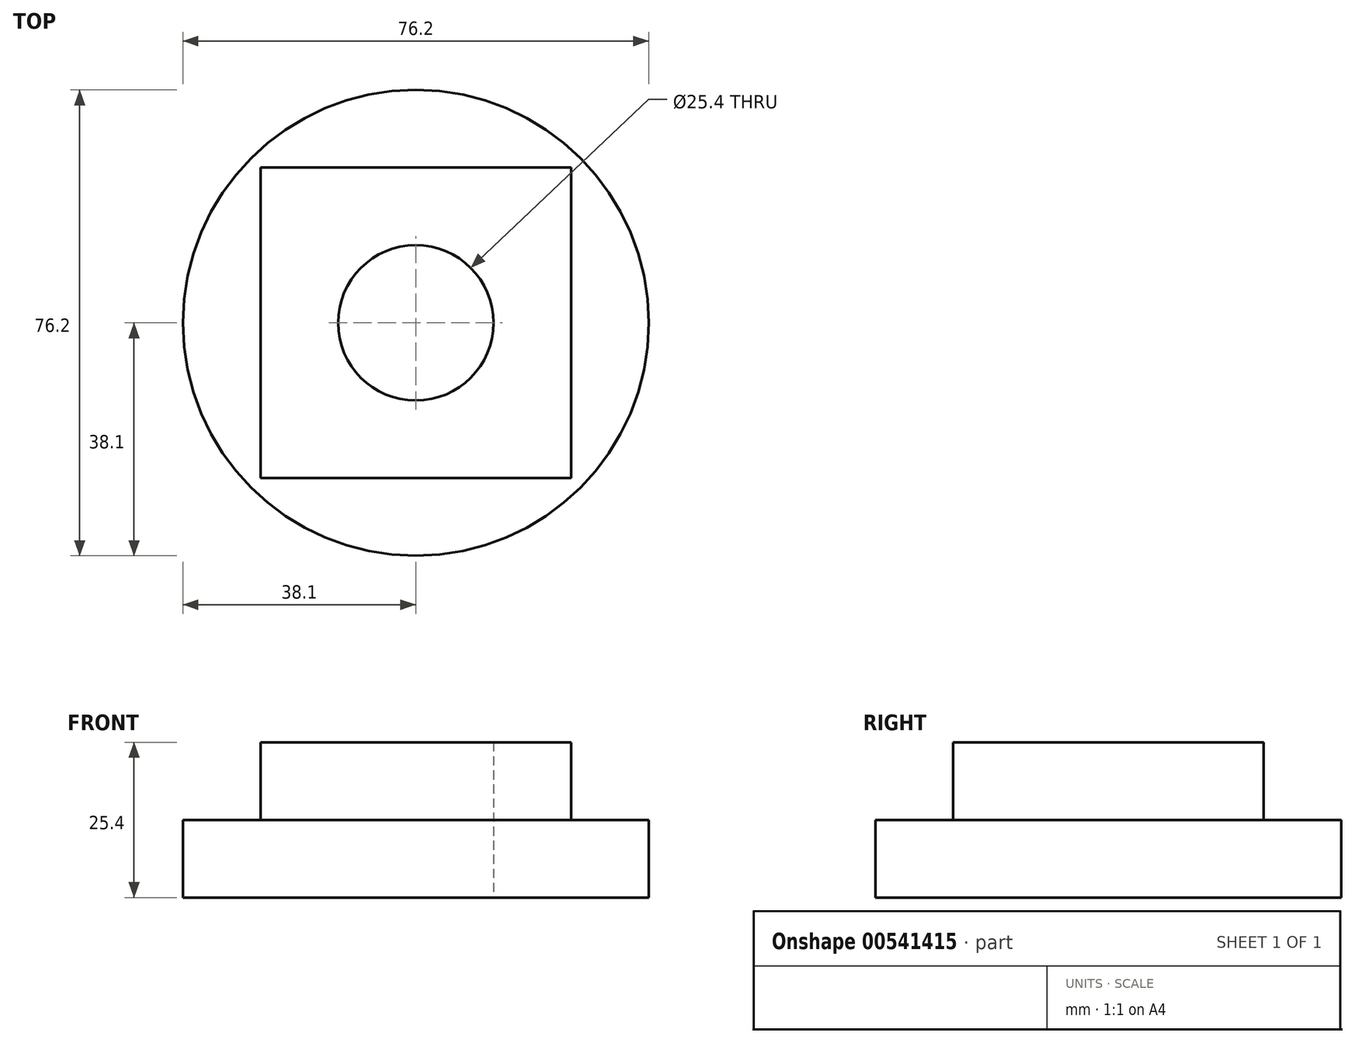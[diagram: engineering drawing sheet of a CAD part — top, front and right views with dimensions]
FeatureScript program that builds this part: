
annotation { "Feature Type Name" : "Feature", "Feature Type Description" : "" }
export const myFeature = defineFeature(function(context is Context, id is Id, definition is map)
    precondition{}
    {
        {
            var Q0;
            Q0=qCreatedBy(makeId("Top.planeOp"),FACE);
            var sketch = newSketch(context, id + "F0", { "sketchPlane" : qUnion([Q0])});
            skCircle(sketch, "E0", {"center": v(0, 0) * mm, "radius": 38.1 * mm});
            skLineSegment(sketch, "E1.bottom", {"start": v(-25.4, 25.4) * mm, "end": v(25.4, 25.4) * mm});
            skLineSegment(sketch, "E1.top", {"start": v(-25.4, -25.4) * mm, "end": v(25.4, -25.4) * mm});
            skLineSegment(sketch, "E1.left", {"start": v(-25.4, 25.4) * mm, "end": v(-25.4, -25.4) * mm});
            skLineSegment(sketch, "E1.right", {"start": v(25.4, 25.4) * mm, "end": v(25.4, -25.4) * mm});
            skCircle(sketch, "E2", {"center": v(0, 0) * mm, "radius": 12.7 * mm});
            skSolve(sketch);
        }
        {
            var Q0;
            Q0=makeQuery(id+"F0.imprint","IMPRINT",FACE,{"disambiguationData":[TD([[makeQuery(id+"F0.imprint","IMPRINT",EDGE,{"derivedFrom":sQuery(id+"F0.wireOp",EDGE,"E0")}),1.0]])]});
            var Q1;
            Q1=makeQuery(id+"F0.imprint","IMPRINT",FACE,{"disambiguationData":[TD([[makeQuery(id+"F0.imprint","IMPRINT",EDGE,{"derivedFrom":sQuery(id+"F0.wireOp",EDGE,"E1.bottom")}),-1.0]])]});
            var Q2;
            Q2=makeQuery(id+"F0.imprint","IMPRINT",FACE,{"disambiguationData":[TD([[makeQuery(id+"F0.imprint","IMPRINT",EDGE,{"derivedFrom":sQuery(id+"F0.wireOp",EDGE,"E2")}),1.0]])]});
            extrude(context, id + "F1", {"entities" : qUnion([Q0, Q1, Q2]), "depth" : 12.7 * mm, "offsetDistance" : 25.4 * mm});
        }
        {
            var Q0;
            Q0=qCreatedBy(makeId("Top.planeOp"),FACE);
            var sketch = newSketch(context, id + "F2", { "sketchPlane" : qUnion([Q0])});
            skLineSegment(sketch, "E3.bottom", {"start": v(-25.4, 25.4) * mm, "end": v(25.4, 25.4) * mm});
            skLineSegment(sketch, "E3.top", {"start": v(-25.4, -25.4) * mm, "end": v(25.4, -25.4) * mm});
            skLineSegment(sketch, "E3.left", {"start": v(-25.4, 25.4) * mm, "end": v(-25.4, -25.4) * mm});
            skLineSegment(sketch, "E3.right", {"start": v(25.4, 25.4) * mm, "end": v(25.4, -25.4) * mm});
            skPoint(sketch, "E3.middle", {"position": v(0, 0) * mm});
            skSolve(sketch);
        }
        {
            var Q0;
            Q0 = qSketchRegion(id + "F2", true);
            extrude(context, id + "F3", {"entities" : qUnion([Q0]), "operationType" : NewBodyOperationType.ADD, "depth" : 25.4 * mm, "offsetDistance" : 25.4 * mm});
        }
        {
            var Q0;
            Q0=qCreatedBy(makeId("Top.planeOp"),FACE);
            var sketch = newSketch(context, id + "F4", { "sketchPlane" : qUnion([Q0])});
            skCircle(sketch, "E4", {"center": v(0, 0) * mm, "radius": 12.7 * mm});
            skSolve(sketch);
        }
        {
            var Q0;
            Q0 = qSketchRegion(id + "F4", true);
            extrude(context, id + "F5", {"entities" : qUnion([Q0]), "operationType" : NewBodyOperationType.REMOVE, "depth" : 25.4 * mm, "offsetDistance" : 25.4 * mm});
        }
    });
